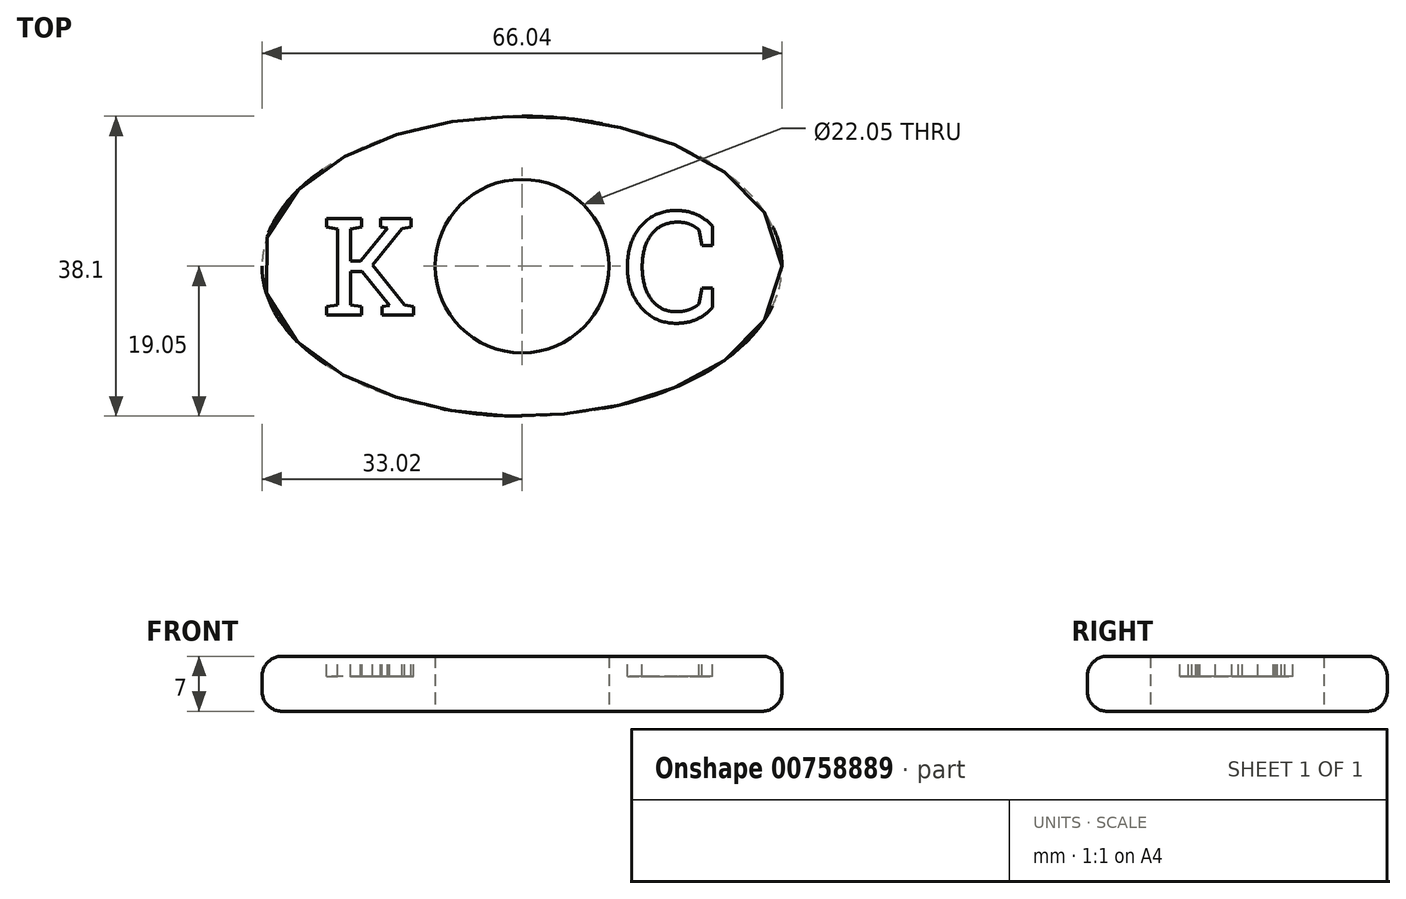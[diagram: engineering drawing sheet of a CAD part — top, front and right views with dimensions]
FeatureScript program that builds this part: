
annotation { "Feature Type Name" : "Feature", "Feature Type Description" : "" }
export const myFeature = defineFeature(function(context is Context, id is Id, definition is map)
    precondition{}
    {
        {
            var Q0;
            Q0=qCreatedBy(makeId("Top.planeOp"),FACE);
            var sketch = newSketch(context, id + "F0", { "sketchPlane" : qUnion([Q0])});
            skEllipse(sketch, "E0", {"center": v(0, 0) * mm, "majorRadius": 33.02 * mm, "minorRadius": 19.05 * mm, "majorAxis": v(1, 0)});
            skCircle(sketch, "E1", {"center": v(0, 0) * mm, "radius": 11.03 * mm});
            skLineSegment(sketch, "E2", {"start": v(-33.02, 0) * mm, "end": v(33.02, 0) * mm, "construction": true});
            skLineSegment(sketch, "E3", {"start": v(0, 19.05) * mm, "end": v(0, -19.05) * mm, "construction": true});
            skSolve(sketch);
        }
        {
            var Q0;
            Q0=makeQuery(id+"F0.imprint","IMPRINT",FACE,{"disambiguationData":[TD([[makeQuery(id+"F0.imprint","IMPRINT",EDGE,{"derivedFrom":sQuery(id+"F0.wireOp",EDGE,"E0")}),1.0]])]});
            extrude(context, id + "F1", {"entities" : qUnion([Q0]), "depth" : 7 * mm, "offsetDistance" : 25.4 * mm});
        }
        {
            var Q0;
            Q0=makeQuery(id+"F1.opExtrude","CAP_EDGE",EDGE,{"disambiguationData":[OSD([sQuery(id+"F0.wireOp",EDGE,"E0")])],"isStart":false});
            var Q1;
            Q1=makeQuery(id+"F1.opExtrude","CAP_EDGE",EDGE,{"disambiguationData":[OSD([sQuery(id+"F0.wireOp",EDGE,"E0")])],"isStart":true});
            fillet(context, id + "F2", {"entities" : qUnion([Q0, Q1]), "radius" : 2.54 * mm, "tangentPropagation" : true, "allowEdgeOverflow" : false});
        }
        {
            var Q0;
            Q0=makeQuery(id+"F1.opExtrude","CAP_FACE",FACE,{"disambiguationData":[OSD([sQuery(id+"F0.wireOp",EDGE,"E0"),sQuery(id+"F0.wireOp",EDGE,"E1")])],"isStart":false});
            var sketch = newSketch(context, id + "F3", { "sketchPlane" : qUnion([Q0])});
            skSolve(sketch);
        }
        {
            var Q0;
            {var subQ0=sQuery(id+"F0.wireOp",EDGE,"E1");Q0=makeQuery(id+"F3.imprint","IMPRINT",FACE,{"disambiguationData":[TD([[makeQuery(id+"F3.imprint","IMPRINT",EDGE,{"derivedFrom":makeQuery(id+"F1.opExtrude","CAP_EDGE",EDGE,{"disambiguationData":[OSD([subQ0])],"isStart":false})}),-1.0]])]});}
            var sketch = newSketch(context, id + "F4", { "sketchPlane" : qUnion([Q0])});
            skText(sketch, "E4", { "text": "K", "fontName": "RobotoSlab-Regular.ttf"});
            skText(sketch, "E5", { "text": "C", "fontName": "RobotoSlab-Regular.ttf"});
            skLineSegment(sketch, "E6", {"start": v(0, 0) * mm, "end": v(-25.4, 0) * mm, "construction": true});
            skLineSegment(sketch, "E7", {"start": v(0, 0) * mm, "end": v(25.4, 0) * mm, "construction": true});
            skLineSegment(sketch, "E8", {"start": v(-25.4, 0) * mm, "end": v(-12.7, 0) * mm, "construction": true});
            skLineSegment(sketch, "E9", {"start": v(12.7, 0) * mm, "end": v(25.4, 0) * mm});
            skPoint(sketch, "E10", {"position": v(19.05, 0) * mm});
            skLineSegment(sketch, "E11", {"start": v(12.7, 0) * mm, "end": v(25.4, 0) * mm, "construction": true});
            skPoint(sketch, "E12", {"position": v(-19.05, 0) * mm});
            const initialGuessF4  = {"E4": [-0.0254, -0.0062, 1, 0, 0.0124], "E5": [0.0127, -0.00706, 1, 0, 0.01411]};
            skSetInitialGuess(sketch, initialGuessF4);
            skSolve(sketch);
        }
        {
            var Q0;
            Q0 = qSketchRegion(id + "F4", true);
            extrude(context, id + "F5", {"entities" : qUnion([Q0]), "operationType" : NewBodyOperationType.REMOVE, "oppositeDirection" : true, "depth" : 2.54 * mm, "offsetDistance" : 25.4 * mm});
        }
    });
